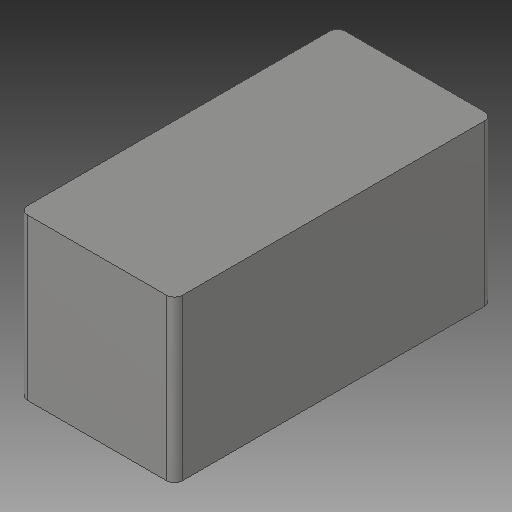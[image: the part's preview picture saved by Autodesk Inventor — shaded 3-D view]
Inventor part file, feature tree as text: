
AUTODESK INVENTOR PART (.ipt)
format: ipt  version: 2017 (Build 210142000, 142)  size: 84,480 bytes
history: native  units: in
note: dims shown in document units (in); Inventor stores cm internally (conversion verified against a paired STEP export)
features: fillet x1
ambient origin geometry x8: Origin, YZ Plane, XZ Plane, XY Plane, X Axis, Y Axis, Z Axis, Center Point
bodies: Solid1 (feature_tree)
feature tree (1):
  fillet  "Fillet1"  [1 undecoded]
note: 1 required parameter value undecoded (feature->parameter linkage not recoverable at this tier; creation-order binding heuristic only, values carry confidence <= 0.55)
